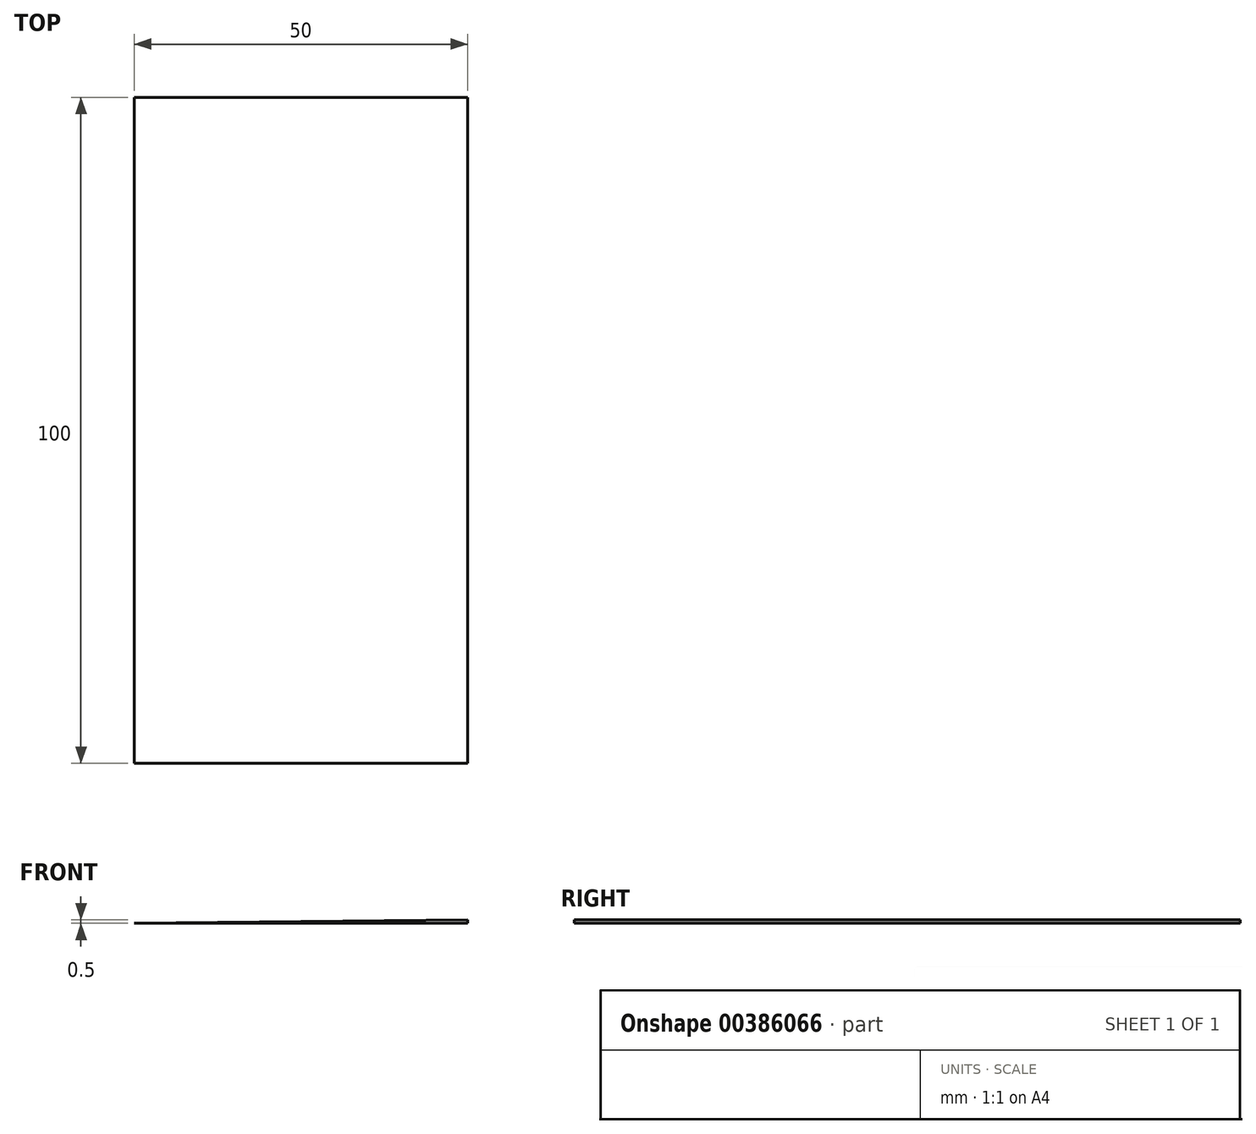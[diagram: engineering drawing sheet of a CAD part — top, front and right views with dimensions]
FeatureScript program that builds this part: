
annotation { "Feature Type Name" : "Feature", "Feature Type Description" : "" }
export const myFeature = defineFeature(function(context is Context, id is Id, definition is map)
    precondition{}
    {
        {
            var Q0;
            Q0=qCreatedBy(makeId("Front.planeOp"),FACE);
            var sketch = newSketch(context, id + "F0", { "sketchPlane" : qUnion([Q0])});
            skLineSegment(sketch, "E0", {"start": v(-60.21, 0) * mm, "end": v(-10.21, 0) * mm});
            skLineSegment(sketch, "E1", {"start": v(-10.21, 0) * mm, "end": v(-10.21, 0.5) * mm});
            skLineSegment(sketch, "E2", {"start": v(-10.21, 0.5) * mm, "end": v(-60.21, 0) * mm});
            skSolve(sketch);
        }
        {
            var Q0;
            Q0=makeQuery(id+"F0.imprint","IMPRINT",FACE,{"disambiguationData":[TD([[makeQuery(id+"F0.imprint","IMPRINT",EDGE,{"derivedFrom":sQuery(id+"F0.wireOp",EDGE,"E0")}),1.0]])]});
            extrude(context, id + "F1", {"entities" : qUnion([Q0]), "depth" : 100 * mm});
        }
    });
